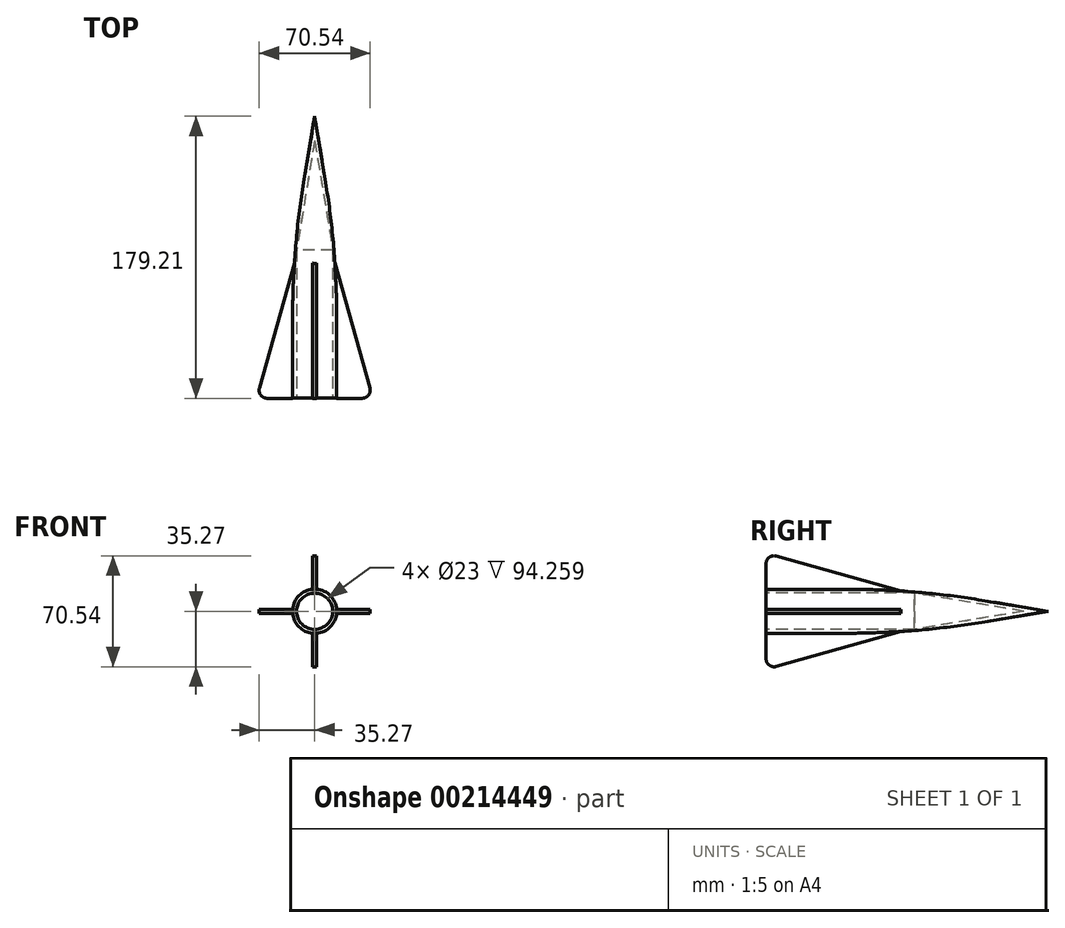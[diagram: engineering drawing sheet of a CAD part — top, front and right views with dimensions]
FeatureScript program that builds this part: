
annotation { "Feature Type Name" : "Feature", "Feature Type Description" : "" }
export const myFeature = defineFeature(function(context is Context, id is Id, definition is map)
    precondition{}
    {
        {
            var Q0;
            Q0=qCreatedBy(makeId("Top.planeOp"),FACE);
            var sketch = newSketch(context, id + "F0", { "sketchPlane" : qUnion([Q0])});
            skLineSegment(sketch, "E0", {"start": v(0, 118.41) * mm, "end": v(-14.04, 33.49) * mm});
            skLineSegment(sketch, "E1", {"start": v(-14.04, 33.49) * mm, "end": v(-14.04, -93.51) * mm});
            skLineSegment(sketch, "E2", {"start": v(-14.04, -93.51) * mm, "end": v(-11.5, -93.51) * mm});
            skLineSegment(sketch, "E3", {"start": v(-11.5, -93.51) * mm, "end": v(-11.5, 33.49) * mm});
            skLineSegment(sketch, "E4", {"start": v(-11.5, 33.49) * mm, "end": v(0, 103.05) * mm});
            skLineSegment(sketch, "E5", {"start": v(0, 103.05) * mm, "end": v(0, 118.41) * mm});
            skSolve(sketch);
        }
        {
            var Q0;
            Q0 = qSketchRegion(id + "F0", true);
            var Q1;
            Q1=sQuery(id+"F0.wireOp",EDGE,"E5");
            revolve(context, id + "F1", {"entities" : qUnion([Q0]), "axis" : qUnion([Q1]), "revolveType" : RevolveType.FULL});
        }
        {
            var Q0;
            Q0=makeQuery(id+"F1.opRevolve","SWEPT_EDGE",EDGE,{"disambiguationData":[OSD([sQuery(id+"F0.wireOp",EDGE,"E0"),sQuery(id+"F0.wireOp",EDGE,"E1")])]});
            fillet(context, id + "F2", {"entities" : qUnion([Q0]), "radius" : 528.38 * mm, "tangentPropagation" : true, "allowEdgeOverflow" : false});
        }
        {
            var Q0;
            Q0=qCreatedBy(makeId("Top.planeOp"),FACE);
            var sketch = newSketch(context, id + "F3", { "sketchPlane" : qUnion([Q0])});
            skLineSegment(sketch, "E6", {"start": v(12.2, -63.34) * mm, "end": v(37.6, -63.34) * mm});
            skLineSegment(sketch, "E7", {"start": v(37.6, -63.34) * mm, "end": v(12.67, 25.56) * mm});
            skLineSegment(sketch, "E8", {"start": v(12.67, 25.56) * mm, "end": v(12.2, -63.34) * mm});
            skSolve(sketch);
        }
        {
            var Q0;
            Q0=makeQuery(id+"F3.imprint","IMPRINT",FACE,{"disambiguationData":[TD([[makeQuery(id+"F3.imprint","IMPRINT",EDGE,{"derivedFrom":sQuery(id+"F3.wireOp",EDGE,"E6")}),1.0]])]});
            extrude(context, id + "F4", {"entities" : qUnion([Q0]), "operationType" : NewBodyOperationType.ADD, "endBound" : BoundingType.SYMMETRIC, "depth" : 2.54 * mm});
        }
        {
            var Q0;
            Q0=makeQuery(id+"F1.opRevolve","SWEPT_BODY",BODY,{"disambiguationData":[OSD([sQuery(id+"F0.wireOp",EDGE,"E0"),sQuery(id+"F0.wireOp",EDGE,"E1"),sQuery(id+"F0.wireOp",EDGE,"E2"),sQuery(id+"F0.wireOp",EDGE,"E3"),sQuery(id+"F0.wireOp",EDGE,"E4"),sQuery(id+"F0.wireOp",EDGE,"E5")])]});
            var Q1;
            Q1=makeQuery(id+"F1.opRevolve","SWEPT_EDGE",EDGE,{"disambiguationData":[OSD([sQuery(id+"F0.wireOp",EDGE,"E2"),sQuery(id+"F0.wireOp",EDGE,"E3")])]});
            circularPattern(context, id + "F5", {"entities" : qUnion([Q0]), "axis" : qUnion([Q1]), "angle" : 360 * degree, "instanceCount" : 4, "equalSpace" : true});
        }
        {
            var Q0;
            Q0=makeQuery(id+"F1.opRevolve","SWEPT_FACE",FACE,{"disambiguationData":[OSD([sQuery(id+"F0.wireOp",EDGE,"E2")])]});
            extrude(context, id + "F6", {"entities" : qUnion([Q0]), "operationType" : NewBodyOperationType.REMOVE, "oppositeDirection" : true, "depth" : 25.4 * mm});
        }
        {
            var Q0;
            Q0=makeQuery(id+"F6.boolean.opBoolean","COPY",FACE,{"derivedFrom":makeQuery(id+"F6.opExtrude","CAP_FACE",FACE,{"disambiguationData":[OSD([sQuery(id+"F0.wireOp",EDGE,"E2")])],"isStart":false})});
            extrude(context, id + "F7", {"entities" : qUnion([Q0]), "operationType" : NewBodyOperationType.REMOVE, "oppositeDirection" : true, "depth" : 7.34 * mm});
        }
        {
            var Q0;
            Q0=makeQuery(id+"F5.opPattern","COPY",FACE,{"derivedFrom":makeQuery(id+"F4.opExtrude","SWEPT_FACE",FACE,{"disambiguationData":[OSD([sQuery(id+"F3.wireOp",EDGE,"E6")])]}),"instanceName":"1"});
            var Q1;
            Q1=makeQuery(id+"F5.opPattern","COPY",FACE,{"derivedFrom":makeQuery(id+"F4.opExtrude","SWEPT_FACE",FACE,{"disambiguationData":[OSD([sQuery(id+"F3.wireOp",EDGE,"E6")])]}),"instanceName":"3"});
            var Q2;
            Q2=makeQuery(id+"F5.opPattern","COPY",FACE,{"derivedFrom":makeQuery(id+"F4.opExtrude","SWEPT_FACE",FACE,{"disambiguationData":[OSD([sQuery(id+"F3.wireOp",EDGE,"E6")])]}),"instanceName":"2"});
            var Q3;
            Q3=makeQuery(id+"F4.opExtrude","SWEPT_FACE",FACE,{"disambiguationData":[OSD([sQuery(id+"F3.wireOp",EDGE,"E6")])]});
            extrude(context, id + "F8", {"entities" : qUnion([Q0, Q1, Q2, Q3]), "operationType" : NewBodyOperationType.REMOVE, "oppositeDirection" : true, "depth" : 2.54 * mm});
        }
        {
            var Q0;
            {var subQ0=sQuery(id+"F3.wireOp",EDGE,"E6");Q0=makeQuery(id+"F8.boolean.opBoolean","INTERSECT",EDGE,{"derivedFrom":[makeQuery(id+"F4.opExtrude","SWEPT_FACE",FACE,{"disambiguationData":[OSD([sQuery(id+"F3.wireOp",EDGE,"E7")])]}),makeQuery(id+"F8.opExtrude","CAP_FACE",FACE,{"disambiguationData":[OSD([subQ0]),TDD([makeQuery(id+"F4.opExtrude","SWEPT_FACE",FACE,{"disambiguationData":[OSD([subQ0])]})])],"isStart":false})]});}
            var Q1;
            {var subQ0=sQuery(id+"F3.wireOp",EDGE,"E6");Q1=makeQuery(id+"F8.boolean.opBoolean","INTERSECT",EDGE,{"derivedFrom":[makeQuery(id+"F5.opPattern","COPY",FACE,{"derivedFrom":makeQuery(id+"F4.opExtrude","SWEPT_FACE",FACE,{"disambiguationData":[OSD([sQuery(id+"F3.wireOp",EDGE,"E7")])]}),"instanceName":"3"}),makeQuery(id+"F8.opExtrude","CAP_FACE",FACE,{"disambiguationData":[OSD([subQ0]),TDD([makeQuery(id+"F5.opPattern","COPY",FACE,{"derivedFrom":makeQuery(id+"F4.opExtrude","SWEPT_FACE",FACE,{"disambiguationData":[OSD([subQ0])]}),"instanceName":"3"})])],"isStart":false})]});}
            var Q2;
            {var subQ0=sQuery(id+"F3.wireOp",EDGE,"E6");Q2=makeQuery(id+"F8.boolean.opBoolean","INTERSECT",EDGE,{"derivedFrom":[makeQuery(id+"F5.opPattern","COPY",FACE,{"derivedFrom":makeQuery(id+"F4.opExtrude","SWEPT_FACE",FACE,{"disambiguationData":[OSD([sQuery(id+"F3.wireOp",EDGE,"E7")])]}),"instanceName":"2"}),makeQuery(id+"F8.opExtrude","CAP_FACE",FACE,{"disambiguationData":[OSD([subQ0]),TDD([makeQuery(id+"F5.opPattern","COPY",FACE,{"derivedFrom":makeQuery(id+"F4.opExtrude","SWEPT_FACE",FACE,{"disambiguationData":[OSD([subQ0])]}),"instanceName":"2"})])],"isStart":false})]});}
            var Q3;
            {var subQ0=sQuery(id+"F3.wireOp",EDGE,"E6");Q3=makeQuery(id+"F8.boolean.opBoolean","INTERSECT",EDGE,{"derivedFrom":[makeQuery(id+"F5.opPattern","COPY",FACE,{"derivedFrom":makeQuery(id+"F4.opExtrude","SWEPT_FACE",FACE,{"disambiguationData":[OSD([sQuery(id+"F3.wireOp",EDGE,"E7")])]}),"instanceName":"1"}),makeQuery(id+"F8.opExtrude","CAP_FACE",FACE,{"disambiguationData":[OSD([subQ0]),TDD([makeQuery(id+"F5.opPattern","COPY",FACE,{"derivedFrom":makeQuery(id+"F4.opExtrude","SWEPT_FACE",FACE,{"disambiguationData":[OSD([subQ0])]}),"instanceName":"1"})])],"isStart":false})]});}
            fillet(context, id + "F9", {"entities" : qUnion([Q0, Q1, Q2, Q3]), "radius" : 5.08 * mm, "tangentPropagation" : true, "allowEdgeOverflow" : false});
        }
    });
